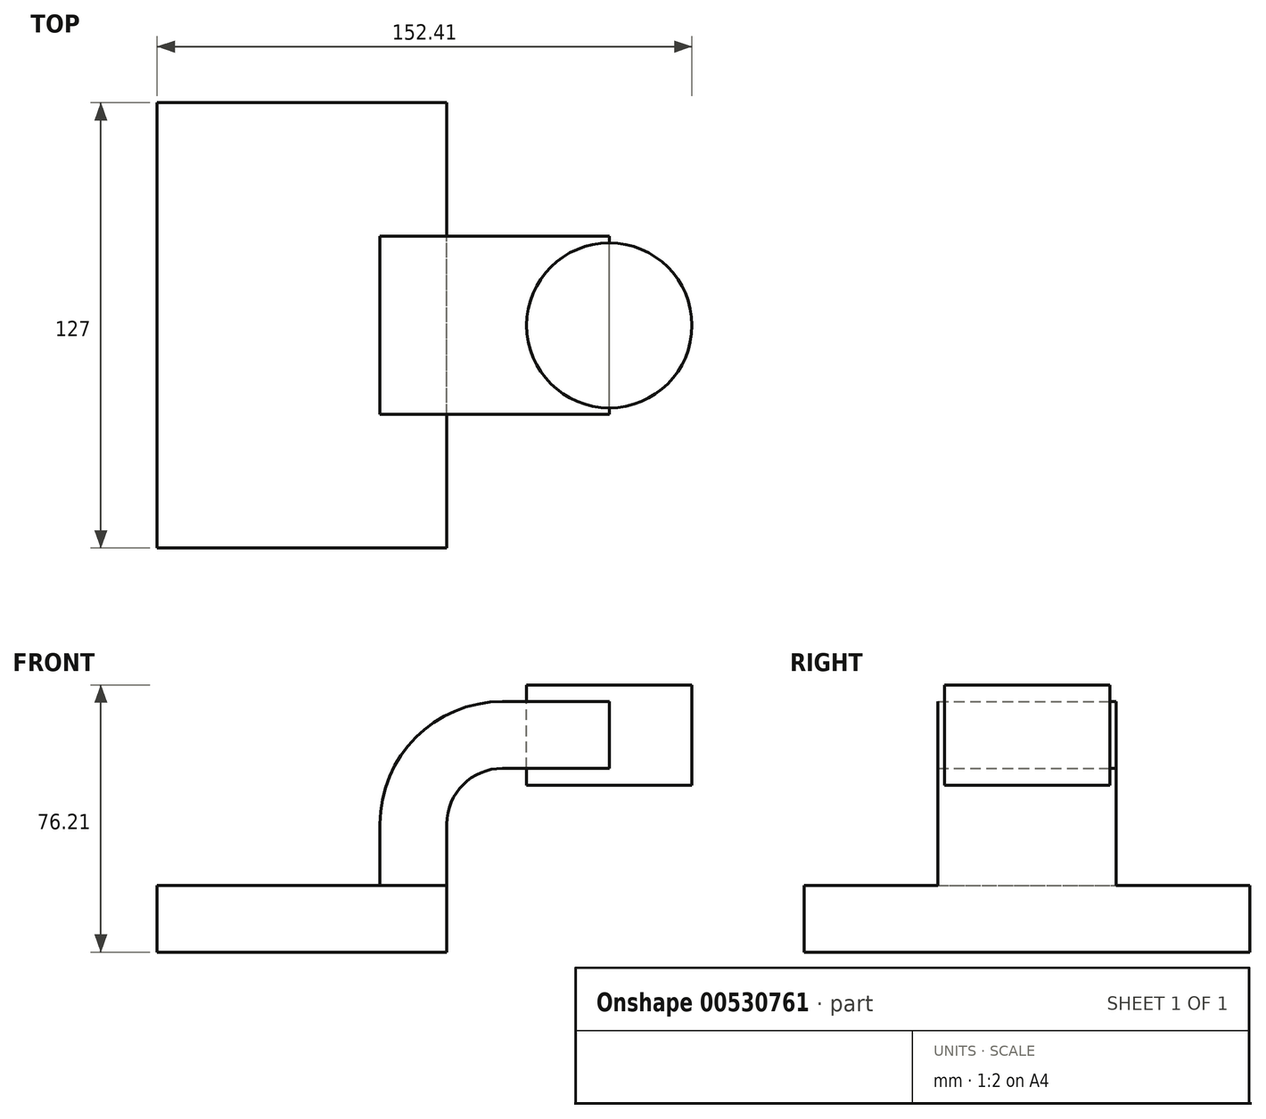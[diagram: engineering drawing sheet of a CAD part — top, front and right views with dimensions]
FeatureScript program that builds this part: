
annotation { "Feature Type Name" : "Feature", "Feature Type Description" : "" }
export const myFeature = defineFeature(function(context is Context, id is Id, definition is map)
    precondition{}
    {
        {
            var Q0;
            Q0=qCreatedBy(makeId("Front.planeOp"),FACE);
            var sketch = newSketch(context, id + "F0", { "sketchPlane" : qUnion([Q0])});
            skLineSegment(sketch, "E0.bottom", {"start": v(-41.28, 9.52) * mm, "end": v(41.27, 9.53) * mm});
            skLineSegment(sketch, "E0.top", {"start": v(-41.28, -9.53) * mm, "end": v(41.28, -9.53) * mm});
            skLineSegment(sketch, "E0.left", {"start": v(-41.28, 9.52) * mm, "end": v(-41.27, -9.53) * mm});
            skLineSegment(sketch, "E0.right", {"start": v(41.28, 9.53) * mm, "end": v(41.28, -9.52) * mm});
            skPoint(sketch, "E0.middle", {"position": v(0, 0) * mm});
            skLineSegment(sketch, "E1.bottom", {"start": v(60.32, 38.1) * mm, "end": v(111.12, 38.1) * mm});
            skLineSegment(sketch, "E1.top", {"start": v(60.32, 66.67) * mm, "end": v(111.12, 66.67) * mm});
            skLineSegment(sketch, "E1.left", {"start": v(60.32, 38.1) * mm, "end": v(60.32, 66.67) * mm});
            skLineSegment(sketch, "E1.right", {"start": v(111.12, 38.1) * mm, "end": v(111.12, 66.67) * mm});
            skPoint(sketch, "E1.middle", {"position": v(85.72, 52.39) * mm});
            skLineSegment(sketch, "E2", {"start": v(41.27, 9.53) * mm, "end": v(41.27, 27) * mm});
            skArc(sketch, "E3", {"start": v(41.27, 27) * mm, "mid": v(45.92, 38.23) * mm, "end": v(57.15, 42.88) * mm});
            skLineSegment(sketch, "E4", {"start": v(57.15, 42.88) * mm, "end": v(87.57, 42.88) * mm});
            skLineSegment(sketch, "E5.0", {"start": v(22.22, 9.53) * mm, "end": v(22.22, 35.2) * mm});
            skArc(sketch, "E6.0", {"start": v(22.22, 27) * mm, "mid": v(32.45, 51.7) * mm, "end": v(57.15, 61.93) * mm});
            skLineSegment(sketch, "E7.0", {"start": v(57.15, 61.93) * mm, "end": v(87.57, 61.93) * mm});
            skLineSegment(sketch, "E8", {"start": v(87.57, 61.93) * mm, "end": v(87.57, 42.88) * mm});
            skFitSpline(sketch, "E9", {"points": [v(-41.28, 9.52) * mm, v(57.15, 61.93) * mm], "startDerivative": vector(45.26, 127.91) * mm, "endDerivative": vector(136.53, -1.45) * mm});
            skLineSegment(sketch, "E10", {"start": v(87.57, 66.67) * mm, "end": v(87.57, 38.1) * mm});
            skPoint(sketch, "E10.startSnap0", {"position": v(87.57, 52.4) * mm});
            skSolve(sketch);
        }
        {
            var Q0;
            Q0=makeQuery(id+"F0.imprint","IMPRINT",FACE,{"disambiguationData":[TD([[makeQuery(id+"F0.imprint","IMPRINT",EDGE,{"derivedFrom":sQuery(id+"F0.wireOp",EDGE,"E0.top")}),1.0]])]});
            extrude(context, id + "F1", {"entities" : qUnion([Q0]), "endBound" : BoundingType.SYMMETRIC, "depth" : 127 * mm, "offsetDistance" : 25.4 * mm});
        }
        {
            var Q0;
            {var subQ1=sQuery(id+"F0.wireOp",EDGE,"E2");Q0=makeQuery(id+"F0.imprint","IMPRINT",FACE,{"disambiguationData":[TD([[makeQuery(id+"F0.imprint","IMPRINT",EDGE,{"derivedFrom":subQ1}),1.0]])]});}
            var Q1;
            {var subQ5=sQuery(id+"F0.wireOp",EDGE,"E8");Q1=makeQuery(id+"F0.imprint","IMPRINT",FACE,{"disambiguationData":[TD([[makeQuery(id+"F0.imprint","IMPRINT",EDGE,{"derivedFrom":subQ5}),-1.0]])]});}
            extrude(context, id + "F2", {"entities" : qUnion([Q0, Q1]), "operationType" : NewBodyOperationType.ADD, "endBound" : BoundingType.SYMMETRIC, "depth" : 50.8 * mm, "offsetDistance" : 25.4 * mm});
        }
        {
            var Q0;
            {var subQ4=sQuery(id+"F0.wireOp",EDGE,"E6.0");Q0=makeQuery(id+"F0.imprint","IMPRINT",FACE,{"disambiguationData":[TD([[makeQuery(id+"F0.imprint","IMPRINT",EDGE,{"derivedFrom":subQ4}),1.0]])]});}
            extrude(context, id + "F3", {"entities" : qUnion([Q0]), "operationType" : NewBodyOperationType.ADD, "depth" : 15.88 * mm, "offsetDistance" : 25.4 * mm});
        }
        {
            var Q0;
            {var subQ0=sQuery(id+"F0.wireOp",EDGE,"E4");var subQ1=sQuery(id+"F0.wireOp",EDGE,"E1.left");var subQ2=makeQuery(id+"F0.imprint","INTERSECT",VERTEX,{"derivedFrom":[subQ1,subQ0]});Q0=makeQuery(id+"F0.imprint","IMPRINT",FACE,{"disambiguationData":[TD([[makeQuery(id+"F0.imprint","IMPRINT",EDGE,{"disambiguationData":[TD([[subQ2,-1.0]])],"derivedFrom":subQ1}),-1.0]])]});}
            extrude(context, id + "F4", {"entities" : qUnion([Q0]), "operationType" : NewBodyOperationType.ADD, "endBound" : BoundingType.SYMMETRIC, "depth" : 50.8 * mm, "offsetDistance" : 25.4 * mm});
        }
        {
            var Q0;
            {var subQ4=sQuery(id+"F0.wireOp",EDGE,"E1.right");Q0=makeQuery(id+"F0.imprint","IMPRINT",FACE,{"disambiguationData":[TD([[makeQuery(id+"F0.imprint","IMPRINT",EDGE,{"derivedFrom":subQ4}),1.0]])]});}
            var Q1;
            Q1=sQuery(id+"F0.wireOp",EDGE,"E10");
            revolve(context, id + "F5", {"entities" : qUnion([Q0]), "axis" : qUnion([Q1]), "revolveType" : RevolveType.FULL});
        }
    });
